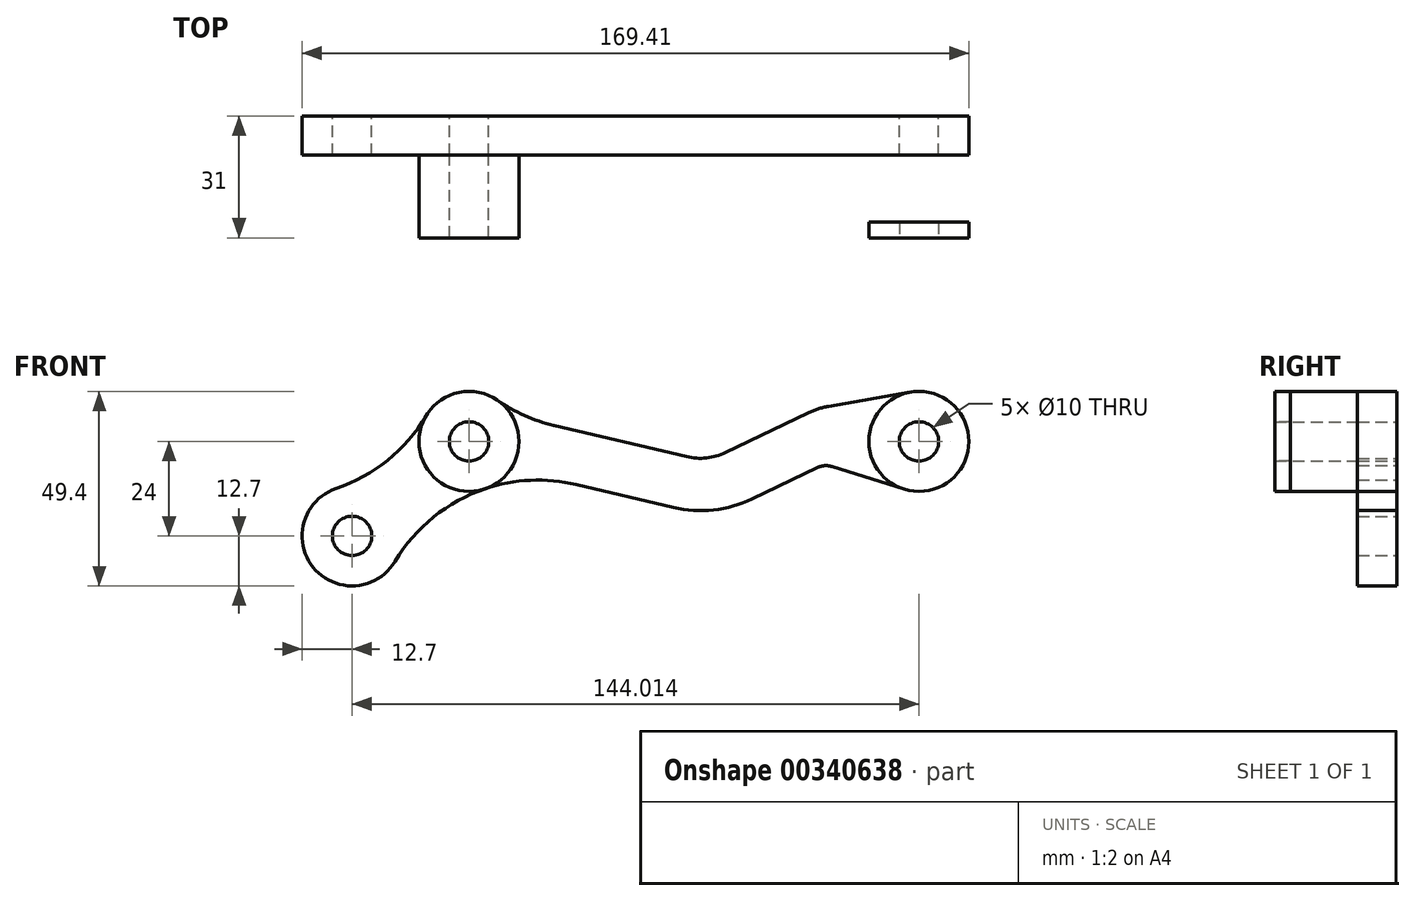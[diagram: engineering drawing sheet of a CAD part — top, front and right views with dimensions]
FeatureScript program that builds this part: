
annotation { "Feature Type Name" : "Feature", "Feature Type Description" : "" }
export const myFeature = defineFeature(function(context is Context, id is Id, definition is map)
    precondition{}
    {
        {
            var Q0;
            Q0=qCreatedBy(makeId("Front.planeOp"),FACE);
            var sketch = newSketch(context, id + "F0", { "sketchPlane" : qUnion([Q0])});
            skCircle(sketch, "E0", {"center": v(15, 15) * mm, "radius": 5 * mm});
            skCircle(sketch, "E1", {"center": v(44.71, 39) * mm, "radius": 5 * mm});
            skCircle(sketch, "E2", {"center": v(159.01, 39) * mm, "radius": 5 * mm});
            skLineSegment(sketch, "E3", {"start": v(155.22, 26.88) * mm, "end": v(136.9, 32.62) * mm});
            skLineSegment(sketch, "E4", {"start": v(133.24, 32.35) * mm, "end": v(116.6, 24.37) * mm});
            skLineSegment(sketch, "E5", {"start": v(96.67, 22.21) * mm, "end": v(71.96, 28.04) * mm});
            skPoint(sketch, "E6.visualSharp", {"position": v(135.01, 33.2) * mm});
            skArc(sketch, "E6.filletArc", {"start": v(136.9, 32.62) * mm, "mid": v(135.04, 32.83) * mm, "end": v(133.24, 32.35) * mm});
            skPoint(sketch, "E7.visualSharp", {"position": v(107.01, 19.78) * mm});
            skArc(sketch, "E7.filletArc", {"start": v(96.67, 22.21) * mm, "mid": v(106.82, 21.59) * mm, "end": v(116.6, 24.37) * mm});
            skArc(sketch, "E8", {"start": v(51.95, 49.44) * mm, "mid": v(42.02, 51.41) * mm, "end": v(33.8, 45.5) * mm});
            skArc(sketch, "E9", {"start": v(156.84, 51.51) * mm, "mid": v(171.69, 38.17) * mm, "end": v(155.22, 26.88) * mm});
            skArc(sketch, "E10", {"start": v(10.95, 27.04) * mm, "mid": v(5.12, 7.02) * mm, "end": v(25.91, 8.5) * mm});
            skLineSegment(sketch, "E11", {"start": v(66.24, 43.07) * mm, "end": v(99.96, 35.12) * mm});
            skLineSegment(sketch, "E12", {"start": v(109.89, 36.2) * mm, "end": v(130.8, 46.22) * mm});
            skPoint(sketch, "E13.visualSharp", {"position": v(55.57, 45.59) * mm});
            skArc(sketch, "E13.filletArc", {"start": v(51.95, 49.44) * mm, "mid": v(58.8, 45.58) * mm, "end": v(66.24, 43.07) * mm});
            skPoint(sketch, "E14", {"position": v(105.11, 33.9) * mm});
            skArc(sketch, "E15.filletArc", {"start": v(99.96, 35.12) * mm, "mid": v(105.02, 34.8) * mm, "end": v(109.89, 36.2) * mm});
            skArc(sketch, "E16.filletArc", {"start": v(136.01, 47.9) * mm, "mid": v(133.34, 47.24) * mm, "end": v(130.8, 46.22) * mm});
            skArc(sketch, "E17.filletArc", {"start": v(10.95, 27.04) * mm, "mid": v(24.03, 34.22) * mm, "end": v(33.8, 45.5) * mm});
            skArc(sketch, "E18.filletArc", {"start": v(71.96, 28.04) * mm, "mid": v(45.74, 25.81) * mm, "end": v(25.91, 8.5) * mm});
            skLineSegment(sketch, "E19", {"start": v(136.01, 47.9) * mm, "end": v(156.84, 51.51) * mm});
            skSolve(sketch);
        }
        {
            var Q0;
            Q0=qCreatedBy(makeId("Front.planeOp"),FACE);
            cPlane(context, id + "F1", {"entities" : qUnion([Q0]), "cplaneType" : CPlaneType.OFFSET, "offset" : 10 * mm, "width" : 150 * mm, "height" : 150 * mm});
        }
        {
            var Q0;
            Q0=qCreatedBy(id+"F1.planeOp",FACE);
            var sketch = newSketch(context, id + "F2", { "sketchPlane" : qUnion([Q0])});
            skCircle(sketch, "E20", {"center": v(44.71, 39) * mm, "radius": 12.7 * mm});
            skCircle(sketch, "E21", {"center": v(44.71, 39) * mm, "radius": 5 * mm});
            skSolve(sketch);
        }
        {
            var Q0;
            Q0=makeQuery(id+"F0.imprint","IMPRINT",FACE,{"disambiguationData":[TD([[makeQuery(id+"F0.imprint","IMPRINT",EDGE,{"derivedFrom":sQuery(id+"F0.wireOp",EDGE,"E0")}),-1.0]])]});
            var Q1;
            Q1=makeQuery(id+"F0.imprint","IMPRINT",FACE,{"disambiguationData":[TD([[makeQuery(id+"F0.imprint","IMPRINT",EDGE,{"derivedFrom":sQuery(id+"F0.wireOp",EDGE,"E1")}),-1.0]])]});
            extrude(context, id + "F3", {"entities" : qUnion([Q0, Q1]), "depth" : 10 * mm});
        }
        {
            var Q0;
            Q0=makeQuery(id+"F2.imprint","IMPRINT",FACE,{"disambiguationData":[TD([[makeQuery(id+"F2.imprint","IMPRINT",EDGE,{"derivedFrom":sQuery(id+"F2.wireOp",EDGE,"E20")}),1.0]])]});
            extrude(context, id + "F4", {"entities" : qUnion([Q0]), "depth" : 21 * mm});
        }
        {
            var Q0;
            Q0=makeQuery(id+"F4.opExtrude","CAP_FACE",FACE,{"disambiguationData":[OSD([sQuery(id+"F2.wireOp",EDGE,"E20"),sQuery(id+"F2.wireOp",EDGE,"E21")])],"isStart":false});
            cPlane(context, id + "F5", {"entities" : qUnion([Q0]), "cplaneType" : CPlaneType.OFFSET, "offset" : 0 * mm, "width" : 150 * mm, "height" : 150 * mm});
        }
        {
            var Q0;
            Q0=qCreatedBy(id+"F5.planeOp",FACE);
            var sketch = newSketch(context, id + "F6", { "sketchPlane" : qUnion([Q0])});
            skCircle(sketch, "E22", {"center": v(159.01, 39) * mm, "radius": 5 * mm});
            skCircle(sketch, "E23", {"center": v(159.01, 39) * mm, "radius": 12.7 * mm});
            skSolve(sketch);
        }
        {
            var Q0;
            Q0=makeQuery(id+"F6.imprint","IMPRINT",FACE,{"disambiguationData":[TD([[makeQuery(id+"F6.imprint","IMPRINT",EDGE,{"derivedFrom":sQuery(id+"F6.wireOp",EDGE,"E22")}),-1.0]])]});
            extrude(context, id + "F7", {"entities" : qUnion([Q0]), "oppositeDirection" : true, "depth" : 4 * mm});
        }
    });
